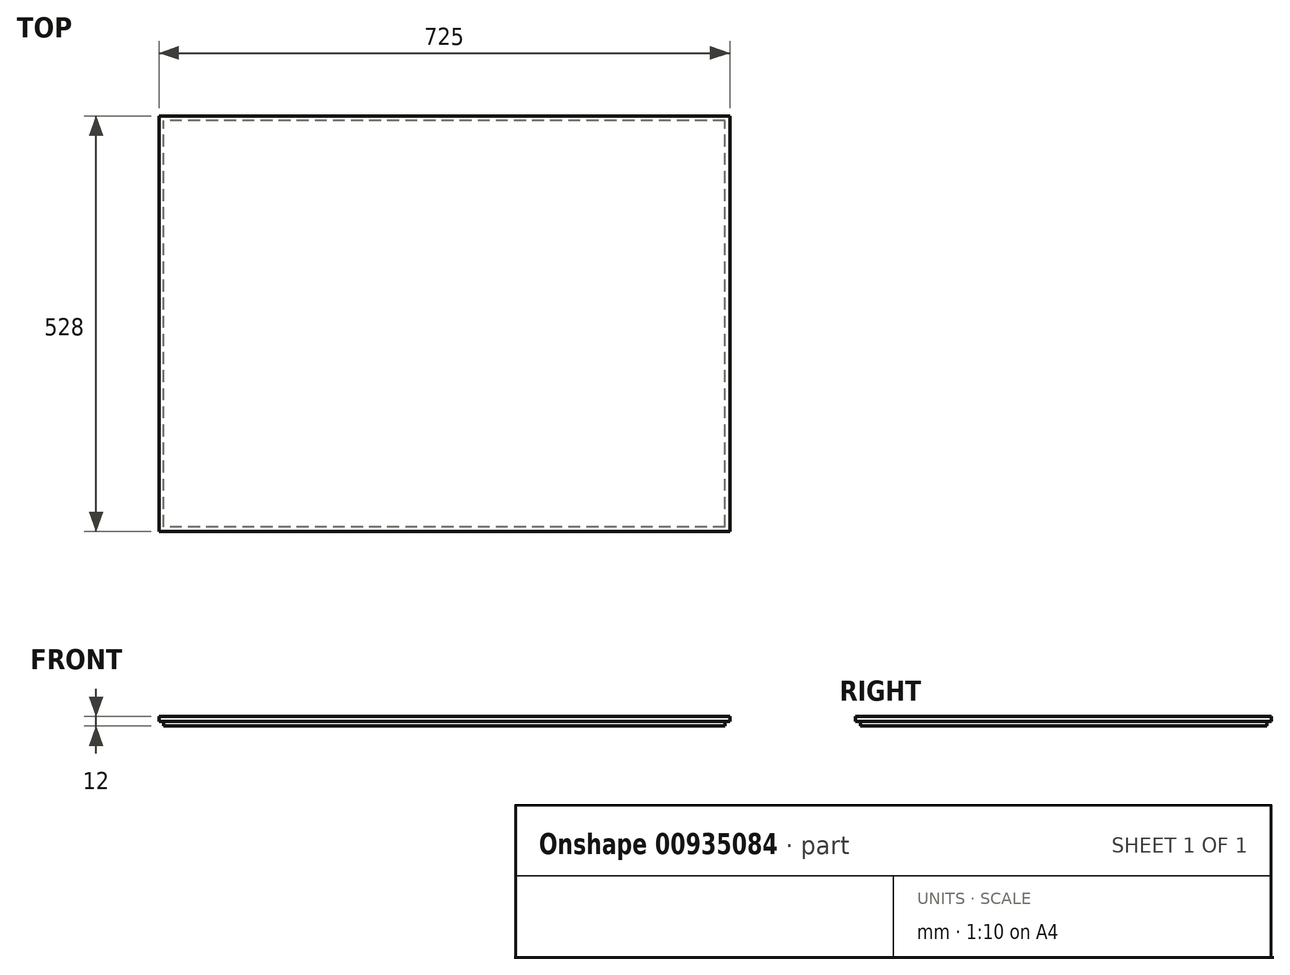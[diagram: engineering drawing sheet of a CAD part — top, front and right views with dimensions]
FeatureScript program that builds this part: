
annotation { "Feature Type Name" : "Feature", "Feature Type Description" : "" }
export const myFeature = defineFeature(function(context is Context, id is Id, definition is map)
    precondition{}
    {
        {
            var Q0;
            Q0=qCreatedBy(makeId("Front.planeOp"),FACE);
            var sketch = newSketch(context, id + "F0", { "sketchPlane" : qUnion([Q0])});
            skLineSegment(sketch, "E0.bottom", {"start": v(0, 0) * mm, "end": v(725, 0) * mm});
            skLineSegment(sketch, "E0.top", {"start": v(0, 12) * mm, "end": v(725, 12) * mm});
            skLineSegment(sketch, "E0.left", {"start": v(0, 0) * mm, "end": v(0, 12) * mm});
            skLineSegment(sketch, "E0.right", {"start": v(725, 0) * mm, "end": v(725, 12) * mm});
            skSolve(sketch);
        }
        {
            var Q0;
            Q0=makeQuery(id+"F0.imprint","IMPRINT",FACE,{"disambiguationData":[TD([[makeQuery(id+"F0.imprint","IMPRINT",EDGE,{"derivedFrom":sQuery(id+"F0.wireOp",EDGE,"E0.bottom")}),1.0]])]});
            extrude(context, id + "F1", {"entities" : qUnion([Q0]), "depth" : 528 * mm, "offsetDistance" : 25 * mm});
        }
        {
            var Q0;
            Q0=qCreatedBy(makeId("Right.planeOp"),FACE);
            var sketch = newSketch(context, id + "F2", { "sketchPlane" : qUnion([Q0])});
            skLineSegment(sketch, "E1.bottom", {"start": v(-528, 6) * mm, "end": v(-522, 6) * mm});
            skLineSegment(sketch, "E1.top", {"start": v(-528, 0) * mm, "end": v(-522, 0) * mm});
            skLineSegment(sketch, "E1.left", {"start": v(-528, 6) * mm, "end": v(-528, 0) * mm});
            skLineSegment(sketch, "E1.right", {"start": v(-522, 6) * mm, "end": v(-522, 0) * mm});
            skLineSegment(sketch, "E2.bottom", {"start": v(0, 6) * mm, "end": v(-6, 6) * mm});
            skLineSegment(sketch, "E2.top", {"start": v(0, 0) * mm, "end": v(-6, 0) * mm});
            skLineSegment(sketch, "E2.left", {"start": v(0, 6) * mm, "end": v(0, 0) * mm});
            skLineSegment(sketch, "E2.right", {"start": v(-6, 6) * mm, "end": v(-6, 0) * mm});
            skLineSegment(sketch, "E3.0", {"start": v(-528, 0) * mm, "end": v(0, 0) * mm, "construction": true});
            skSolve(sketch);
        }
        {
            var Q0;
            Q0=qSketchRegion(id+"F2",true);
            extrude(context, id + "F3", {"entities" : qUnion([Q0]), "operationType" : NewBodyOperationType.REMOVE, "endBound" : BoundingType.THROUGH_ALL, "depth" : 25 * mm, "offsetDistance" : 25 * mm});
        }
        {
            var Q0;
            Q0=qCreatedBy(makeId("Front.planeOp"),FACE);
            var sketch = newSketch(context, id + "F4", { "sketchPlane" : qUnion([Q0])});
            skLineSegment(sketch, "E4.bottom", {"start": v(0, 0) * mm, "end": v(6, 0) * mm});
            skLineSegment(sketch, "E4.top", {"start": v(0, 6) * mm, "end": v(6, 6) * mm});
            skLineSegment(sketch, "E4.left", {"start": v(0, 0) * mm, "end": v(0, 6) * mm});
            skLineSegment(sketch, "E4.right", {"start": v(6, 0) * mm, "end": v(6, 6) * mm});
            skLineSegment(sketch, "E5.bottom", {"start": v(719, 0) * mm, "end": v(725, 0) * mm});
            skLineSegment(sketch, "E5.top", {"start": v(719, 6) * mm, "end": v(725, 6) * mm});
            skLineSegment(sketch, "E5.left", {"start": v(719, 0) * mm, "end": v(719, 6) * mm});
            skLineSegment(sketch, "E5.right", {"start": v(725, 0) * mm, "end": v(725, 6) * mm});
            skSolve(sketch);
        }
        {
            var Q0;
            Q0=qSketchRegion(id+"F4",true);
            extrude(context, id + "F5", {"entities" : qUnion([Q0]), "operationType" : NewBodyOperationType.REMOVE, "endBound" : BoundingType.THROUGH_ALL, "depth" : 25 * mm, "offsetDistance" : 25 * mm});
        }
    });
